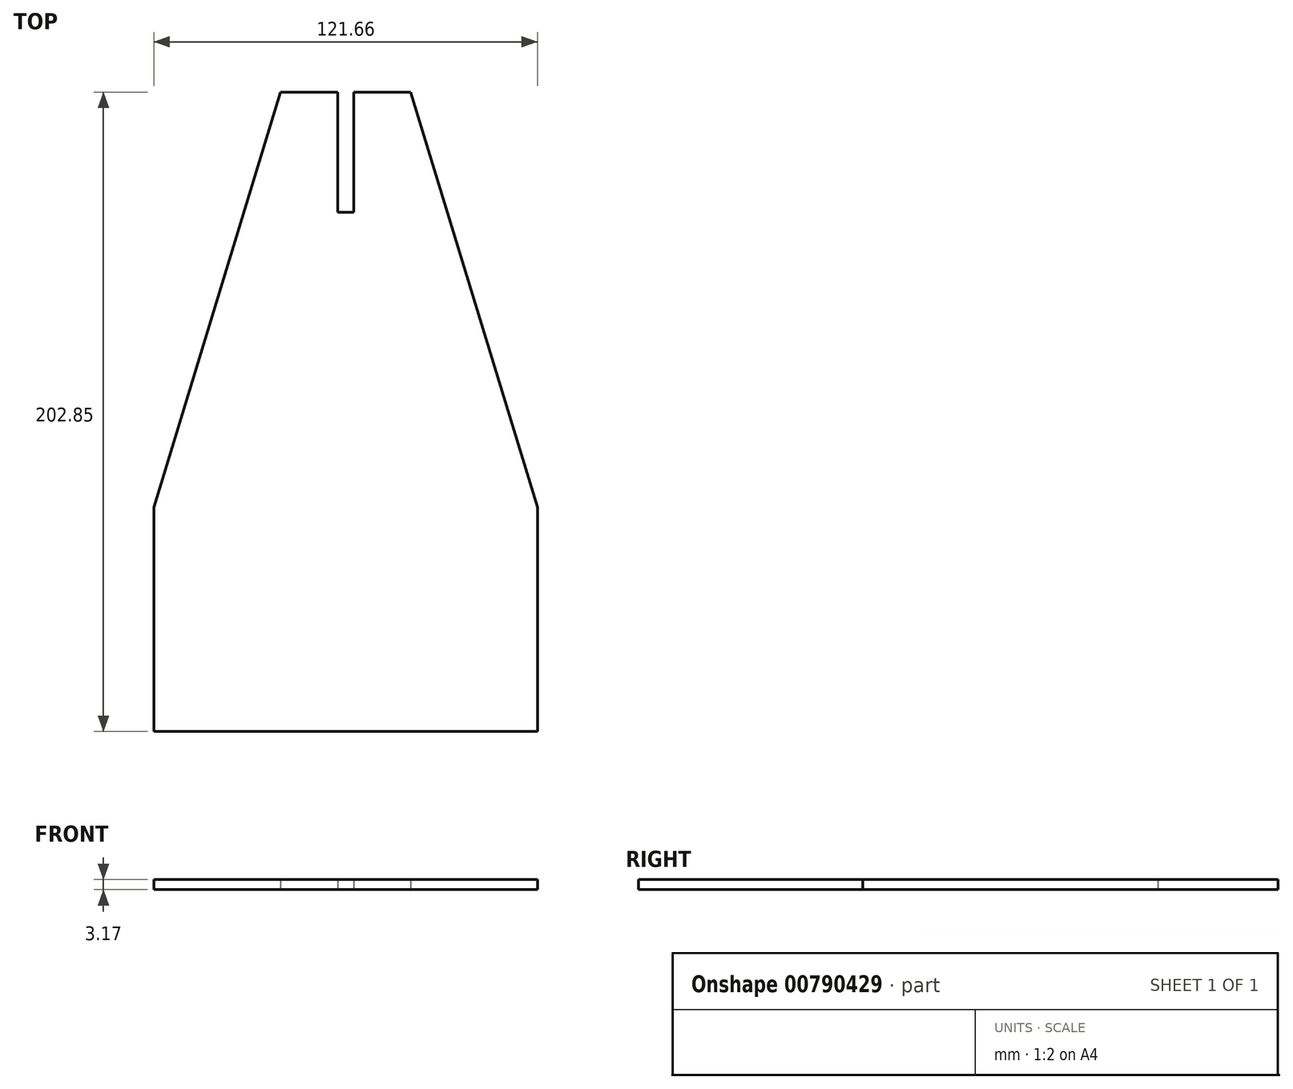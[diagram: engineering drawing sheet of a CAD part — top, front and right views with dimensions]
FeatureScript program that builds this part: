
annotation { "Feature Type Name" : "Feature", "Feature Type Description" : "" }
export const myFeature = defineFeature(function(context is Context, id is Id, definition is map)
    precondition{}
    {
        {
            var Q0;
            Q0=qCreatedBy(makeId("Top.planeOp"),FACE);
            var sketch = newSketch(context, id + "F0", { "sketchPlane" : qUnion([Q0])});
            skLineSegment(sketch, "E0", {"start": v(-20.64, 132.44) * mm, "end": v(-60.83, 0.76) * mm});
            skLineSegment(sketch, "E1", {"start": v(-60.83, -70.4) * mm, "end": v(60.83, -70.4) * mm});
            skLineSegment(sketch, "E2", {"start": v(60.83, 0.76) * mm, "end": v(20.64, 132.44) * mm});
            skLineSegment(sketch, "E3", {"start": v(20.64, 132.44) * mm, "end": v(-20.64, 132.44) * mm});
            skLineSegment(sketch, "E4", {"start": v(0, 132.44) * mm, "end": v(0, -70.4) * mm});
            skPoint(sketch, "E4.endSnap0", {"position": v(0, -70.4) * mm});
            skLineSegment(sketch, "E5", {"start": v(60.83, 0.76) * mm, "end": v(60.83, -70.4) * mm});
            skLineSegment(sketch, "E6", {"start": v(60.83, 0.76) * mm, "end": v(-60.83, 0.76) * mm});
            skLineSegment(sketch, "E7", {"start": v(-60.83, 0.76) * mm, "end": v(-60.83, -70.4) * mm});
            skPoint(sketch, "E8.orphan", {"position": v(-82.55, -70.4) * mm});
            skPoint(sketch, "E9.orphan", {"position": v(82.55, -70.4) * mm});
            skLineSegment(sketch, "E10", {"start": v(-2.54, 132.44) * mm, "end": v(2.54, 132.44) * mm});
            skLineSegment(sketch, "E11", {"start": v(-2.54, 132.44) * mm, "end": v(-2.54, 94.34) * mm});
            skLineSegment(sketch, "E12", {"start": v(2.54, 132.44) * mm, "end": v(2.54, 94.34) * mm});
            skLineSegment(sketch, "E13", {"start": v(2.54, 94.34) * mm, "end": v(-2.54, 94.34) * mm});
            skSolve(sketch);
        }
        {
            var Q0;
            {var subQ0=sQuery(id+"F0.wireOp",EDGE,"E2");Q0=makeQuery(id+"F0.imprint","IMPRINT",FACE,{"disambiguationData":[TD([[makeQuery(id+"F0.imprint","IMPRINT",EDGE,{"derivedFrom":subQ0}),1.0]])]});}
            var Q1;
            {var subQ0=sQuery(id+"F0.wireOp",EDGE,"E0");Q1=makeQuery(id+"F0.imprint","IMPRINT",FACE,{"disambiguationData":[TD([[makeQuery(id+"F0.imprint","IMPRINT",EDGE,{"derivedFrom":subQ0}),1.0]])]});}
            var Q2;
            {var subQ0=sQuery(id+"F0.wireOp",EDGE,"E7");Q2=makeQuery(id+"F0.imprint","IMPRINT",FACE,{"disambiguationData":[TD([[makeQuery(id+"F0.imprint","IMPRINT",EDGE,{"derivedFrom":subQ0}),1.0]])]});}
            var Q3;
            {var subQ0=sQuery(id+"F0.wireOp",EDGE,"E5");Q3=makeQuery(id+"F0.imprint","IMPRINT",FACE,{"disambiguationData":[TD([[makeQuery(id+"F0.imprint","IMPRINT",EDGE,{"derivedFrom":subQ0}),-1.0]])]});}
            extrude(context, id + "F1", {"entities" : qUnion([Q0, Q1, Q2, Q3]), "depth" : 3.17 * mm, "offsetDistance" : 25.4 * mm});
        }
        {
            var Q0;
            {var subQ5=sQuery(id+"F0.wireOp",EDGE,"E11");Q0=makeQuery(id+"F0.imprint","IMPRINT",FACE,{"disambiguationData":[TD([[makeQuery(id+"F0.imprint","IMPRINT",EDGE,{"derivedFrom":subQ5}),1.0]])]});}
            var Q1;
            {var subQ5=sQuery(id+"F0.wireOp",EDGE,"E12");Q1=makeQuery(id+"F0.imprint","IMPRINT",FACE,{"disambiguationData":[TD([[makeQuery(id+"F0.imprint","IMPRINT",EDGE,{"derivedFrom":subQ5}),-1.0]])]});}
            extrude(context, id + "F2", {"entities" : qUnion([Q0, Q1]), "operationType" : NewBodyOperationType.REMOVE, "oppositeDirection" : true, "depth" : 3.17 * mm, "offsetDistance" : 25.4 * mm});
        }
    });
